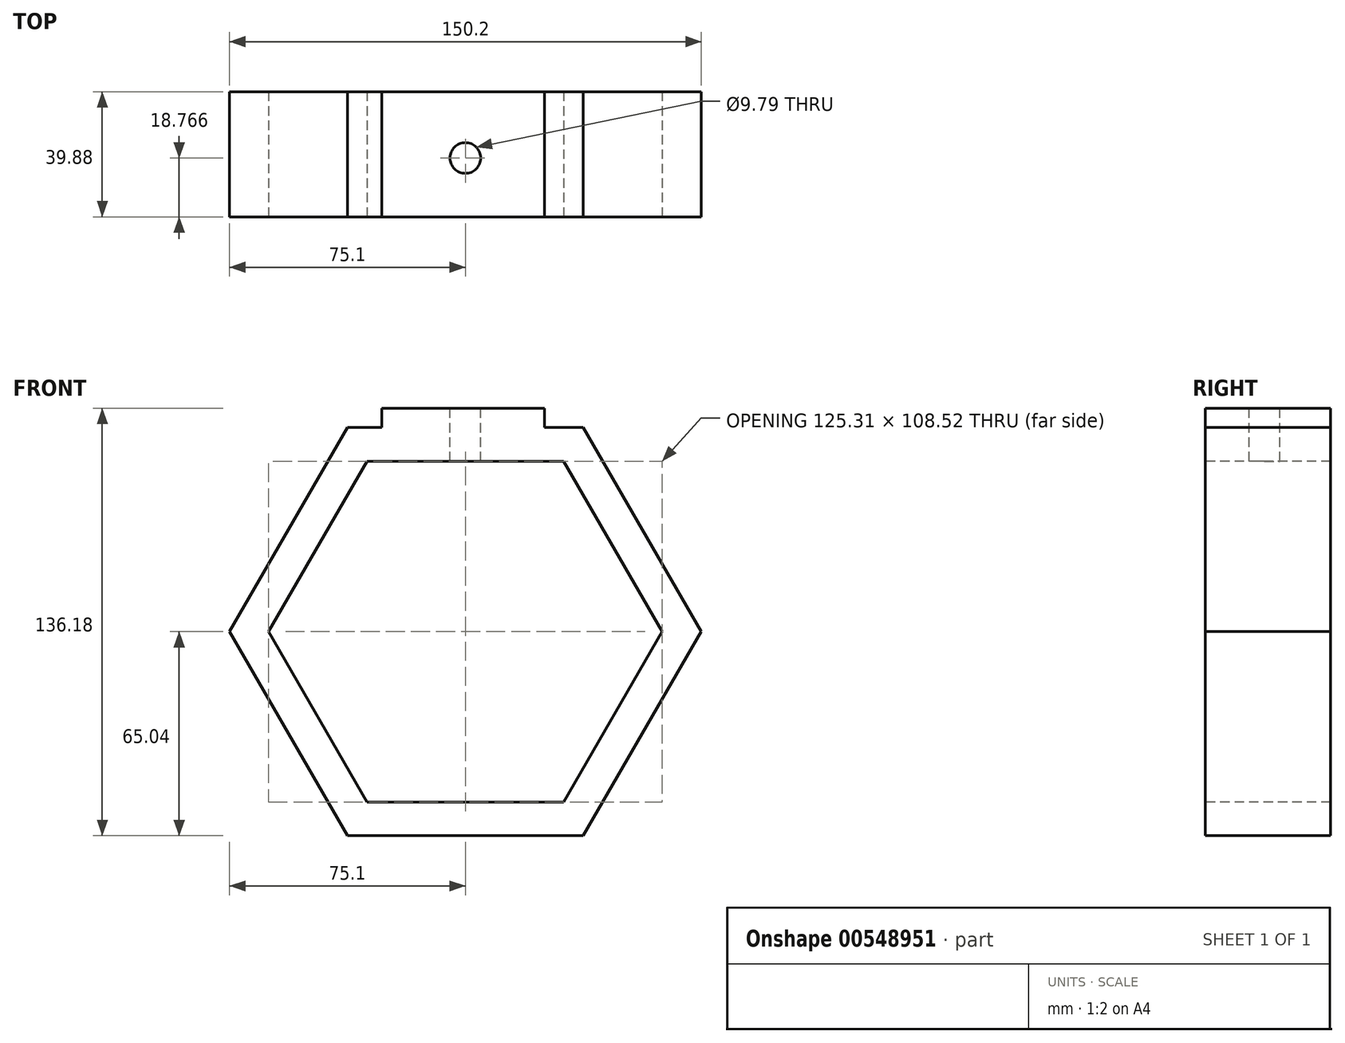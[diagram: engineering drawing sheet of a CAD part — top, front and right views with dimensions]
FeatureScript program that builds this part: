
annotation { "Feature Type Name" : "Feature", "Feature Type Description" : "" }
export const myFeature = defineFeature(function(context is Context, id is Id, definition is map)
    precondition{}
    {
        {
            var Q0;
            Q0=qCreatedBy(makeId("Front.planeOp"),FACE);
            var sketch = newSketch(context, id + "F0", { "sketchPlane" : qUnion([Q0])});
            skCircle(sketch, "E0.cCircle", {"center": v(0, 0) * mm, "radius": 65.04 * mm, "construction": true});
            skLineSegment(sketch, "E0.0", {"start": v(-37.55, 65.04) * mm, "end": v(37.55, 65.04) * mm});
            skLineSegment(sketch, "E0.1", {"start": v(37.55, 65.04) * mm, "end": v(75.1, 0) * mm});
            skLineSegment(sketch, "E0.2", {"start": v(75.1, 0) * mm, "end": v(37.55, -65.04) * mm});
            skLineSegment(sketch, "E0.3", {"start": v(37.55, -65.04) * mm, "end": v(-37.55, -65.04) * mm});
            skLineSegment(sketch, "E0.4", {"start": v(-37.55, -65.04) * mm, "end": v(-75.1, 0) * mm});
            skLineSegment(sketch, "E0.5", {"start": v(-75.1, 0) * mm, "end": v(-37.55, 65.04) * mm});
            skPoint(sketch, "E0.0.midPoint", {"position": v(0, 65.04) * mm});
            skSolve(sketch);
        }
        {
            var Q0;
            Q0=makeQuery(id+"F0.imprint","IMPRINT",FACE,{"disambiguationData":[TD([[makeQuery(id+"F0.imprint","IMPRINT",EDGE,{"derivedFrom":sQuery(id+"F0.wireOp",EDGE,"E0.0")}),-1.0]])]});
            extrude(context, id + "F1", {"entities" : qUnion([Q0]), "depth" : 39.88 * mm, "offsetDistance" : 25.4 * mm});
        }
        {
            var Q0;
            Q0=makeQuery(id+"F1.opExtrude","CAP_FACE",FACE,{"disambiguationData":[OSD([sQuery(id+"F0.wireOp",EDGE,"E0.0"),sQuery(id+"F0.wireOp",EDGE,"E0.1"),sQuery(id+"F0.wireOp",EDGE,"E0.2"),sQuery(id+"F0.wireOp",EDGE,"E0.3"),sQuery(id+"F0.wireOp",EDGE,"E0.4"),sQuery(id+"F0.wireOp",EDGE,"E0.5")])],"isStart":false});
            var sketch = newSketch(context, id + "F2", { "sketchPlane" : qUnion([Q0])});
            skCircle(sketch, "E1.cCircle", {"center": v(0, 0) * mm, "radius": 54.26 * mm, "construction": true});
            skLineSegment(sketch, "E1.0", {"start": v(-31.33, 54.26) * mm, "end": v(31.33, 54.26) * mm});
            skLineSegment(sketch, "E1.1", {"start": v(31.33, 54.26) * mm, "end": v(62.65, 0) * mm});
            skLineSegment(sketch, "E1.2", {"start": v(62.65, 0) * mm, "end": v(31.33, -54.26) * mm});
            skLineSegment(sketch, "E1.3", {"start": v(31.33, -54.26) * mm, "end": v(-31.33, -54.26) * mm});
            skLineSegment(sketch, "E1.4", {"start": v(-31.33, -54.26) * mm, "end": v(-62.65, 0) * mm});
            skLineSegment(sketch, "E1.5", {"start": v(-62.65, 0) * mm, "end": v(-31.33, 54.26) * mm});
            skPoint(sketch, "E1.0.midPoint", {"position": v(0, 54.26) * mm});
            skSolve(sketch);
        }
        {
            var Q0;
            Q0 = qSketchRegion(id + "F2", true);
            extrude(context, id + "F3", {"entities" : qUnion([Q0]), "operationType" : NewBodyOperationType.REMOVE, "oppositeDirection" : true, "depth" : 58.42 * mm, "offsetDistance" : 25.4 * mm});
        }
        {
            var Q0;
            Q0=makeQuery(id+"F1.opExtrude","SWEPT_FACE",FACE,{"disambiguationData":[OSD([sQuery(id+"F0.wireOp",EDGE,"E0.0")])]});
            var sketch = newSketch(context, id + "F4", { "sketchPlane" : qUnion([Q0])});
            skLineSegment(sketch, "E2.bottom", {"start": v(-26.56, 0) * mm, "end": v(25.18, 0) * mm});
            skLineSegment(sketch, "E2.top", {"start": v(-26.56, -39.88) * mm, "end": v(25.18, -39.88) * mm});
            skLineSegment(sketch, "E2.left", {"start": v(-26.56, 0) * mm, "end": v(-26.56, -39.88) * mm});
            skLineSegment(sketch, "E2.right", {"start": v(25.18, 0) * mm, "end": v(25.18, -39.88) * mm});
            skSolve(sketch);
        }
        {
            var Q0;
            Q0=makeQuery(id+"F4.imprint","IMPRINT",FACE,{"disambiguationData":[TD([[makeQuery(id+"F4.imprint","IMPRINT",EDGE,{"derivedFrom":sQuery(id+"F4.wireOp",EDGE,"E2.bottom")}),-1.0]])]});
            extrude(context, id + "F5", {"entities" : qUnion([Q0]), "operationType" : NewBodyOperationType.ADD, "depth" : 6.1 * mm, "offsetDistance" : 25.4 * mm});
        }
        {
            var Q0;
            Q0=makeQuery(id+"F5.opExtrude","CAP_FACE",FACE,{"disambiguationData":[OSD([sQuery(id+"F4.wireOp",EDGE,"E2.bottom"),sQuery(id+"F4.wireOp",EDGE,"E2.top"),sQuery(id+"F4.wireOp",EDGE,"E2.left"),sQuery(id+"F4.wireOp",EDGE,"E2.right")])],"isStart":false});
            var sketch = newSketch(context, id + "F6", { "sketchPlane" : qUnion([Q0])});
            skCircle(sketch, "E3", {"center": v(0, -21.11) * mm, "radius": 4.9 * mm});
            skSolve(sketch);
        }
        {
            var Q0;
            Q0 = qSketchRegion(id + "F6", true);
            extrude(context, id + "F7", {"entities" : qUnion([Q0]), "operationType" : NewBodyOperationType.REMOVE, "oppositeDirection" : true, "depth" : 25.4 * mm, "offsetDistance" : 25.4 * mm});
        }
    });
